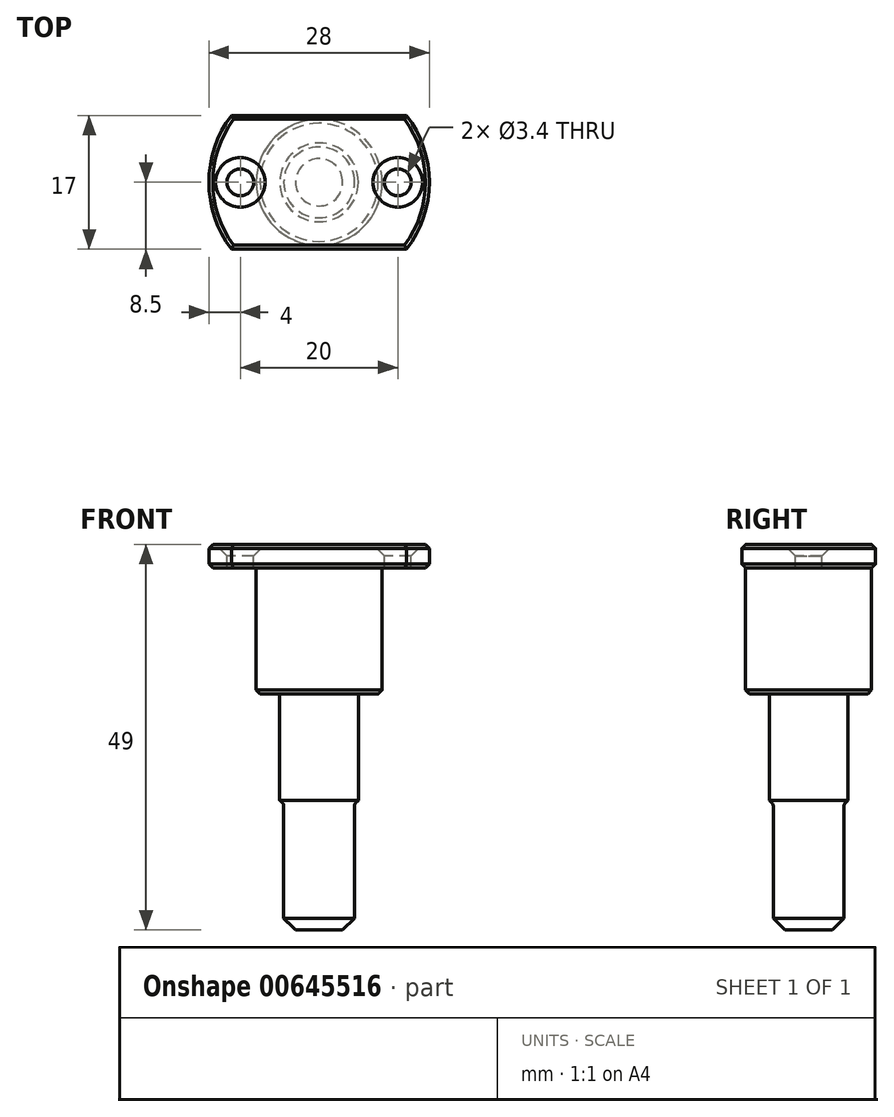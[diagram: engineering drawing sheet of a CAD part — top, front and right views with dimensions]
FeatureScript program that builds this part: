
annotation { "Feature Type Name" : "Feature", "Feature Type Description" : "" }
export const myFeature = defineFeature(function(context is Context, id is Id, definition is map)
    precondition{}
    {
        {
            var Q0;
            Q0=qCreatedBy(makeId("Top.planeOp"),FACE);
            var sketch = newSketch(context, id + "F0", { "sketchPlane" : qUnion([Q0])});
            skCircle(sketch, "E0", {"center": v(0, 0) * mm, "radius": 14 * mm});
            skLineSegment(sketch, "E1", {"start": v(14, 0) * mm, "end": v(14, 8.5) * mm});
            skLineSegment(sketch, "E2.bottom", {"start": v(0, 0) * mm, "end": v(14, 0) * mm});
            skLineSegment(sketch, "E2.top", {"start": v(0, 8.5) * mm, "end": v(14, 8.5) * mm});
            skLineSegment(sketch, "E2.left", {"start": v(0, 0) * mm, "end": v(0, 8.5) * mm});
            skLineSegment(sketch, "E3.MirrorCS", {"start": v(-14, 0) * mm, "end": v(-14, 8.5) * mm});
            skLineSegment(sketch, "E4.MirrorCS", {"start": v(0, 8.5) * mm, "end": v(-14, 8.5) * mm});
            skLineSegment(sketch, "E5.MirrorCS", {"start": v(0, 0) * mm, "end": v(-14, 0) * mm});
            skLineSegment(sketch, "E6.MirrorCS", {"start": v(14, 0) * mm, "end": v(14, -8.5) * mm});
            skLineSegment(sketch, "E7.MirrorCS", {"start": v(-14, 0) * mm, "end": v(-14, -8.5) * mm});
            skLineSegment(sketch, "E8.MirrorCS", {"start": v(0, -8.5) * mm, "end": v(-14, -8.5) * mm});
            skLineSegment(sketch, "E9.MirrorCS", {"start": v(0, -8.5) * mm, "end": v(14, -8.5) * mm});
            skLineSegment(sketch, "E10.MirrorCS", {"start": v(0, 0) * mm, "end": v(0, -8.5) * mm});
            skSolve(sketch);
        }
        {
            var Q0;
            {var subQ0=sQuery(id+"F0.wireOp",EDGE,"E2.left");Q0=makeQuery(id+"F0.imprint","IMPRINT",FACE,{"disambiguationData":[TD([[makeQuery(id+"F0.imprint","IMPRINT",EDGE,{"derivedFrom":subQ0}),1.0]])]});}
            var Q1;
            {var subQ0=sQuery(id+"F0.wireOp",EDGE,"E5.MirrorCS");Q1=makeQuery(id+"F0.imprint","IMPRINT",FACE,{"disambiguationData":[TD([[makeQuery(id+"F0.imprint","IMPRINT",EDGE,{"derivedFrom":subQ0}),1.0]])]});}
            var Q2;
            {var subQ0=sQuery(id+"F0.wireOp",EDGE,"E2.bottom");Q2=makeQuery(id+"F0.imprint","IMPRINT",FACE,{"disambiguationData":[TD([[makeQuery(id+"F0.imprint","IMPRINT",EDGE,{"derivedFrom":subQ0}),-1.0]])]});}
            var Q3;
            {var subQ0=sQuery(id+"F0.wireOp",EDGE,"E2.bottom");Q3=makeQuery(id+"F0.imprint","IMPRINT",FACE,{"disambiguationData":[TD([[makeQuery(id+"F0.imprint","IMPRINT",EDGE,{"derivedFrom":subQ0}),1.0]])]});}
            extrude(context, id + "F1", {"entities" : qUnion([Q0, Q1, Q2, Q3]), "depth" : 3 * mm, "offsetDistance" : 25 * mm});
        }
        {
            var Q0;
            Q0=makeQuery(id+"F1.opExtrude","CAP_FACE",FACE,{"disambiguationData":[OSD([sQuery(id+"F0.wireOp",EDGE,"E2.top"),sQuery(id+"F0.wireOp",EDGE,"E4.MirrorCS"),sQuery(id+"F0.wireOp",EDGE,"E8.MirrorCS"),sQuery(id+"F0.wireOp",EDGE,"E0"),sQuery(id+"F0.wireOp",EDGE,"E9.MirrorCS")])],"isStart":false});
            var sketch = newSketch(context, id + "F2", { "sketchPlane" : qUnion([Q0])});
            skPoint(sketch, "E11", {"position": v(10, 0) * mm});
            skPoint(sketch, "E12.MirrorP", {"position": v(-10, 0) * mm});
            skSolve(sketch);
        }
        {
            var Q0;
            Q0=sQuery(id+"F2.wireOp",VERTEX,"E11");
            var Q1;
            Q1=sQuery(id+"F2.wireOp",VERTEX,"E12.MirrorP");
            var Q2;
            Q2=makeQuery(id+"F1.opExtrude","SWEPT_BODY",BODY,{"disambiguationData":[OSD([sQuery(id+"F0.wireOp",EDGE,"E2.top"),sQuery(id+"F0.wireOp",EDGE,"E4.MirrorCS"),sQuery(id+"F0.wireOp",EDGE,"E8.MirrorCS"),sQuery(id+"F0.wireOp",EDGE,"E0"),sQuery(id+"F0.wireOp",EDGE,"E9.MirrorCS")])]});
            hole(context, id + "F3", {"style" : HoleStyle.C_SINK, "endStyle" : HoleEndStyle.THROUGH, "holeDiameter" : 3.4 * mm, "cSinkDiameter" : 6.3 * mm, "cSinkAngle" : 90 * degree, "majorDiameter" : 5 * mm, "isTappedThrough" : true, "tappedDepth" : 12 * mm, "tapClearance" : 3, "locations" : qUnion([Q0, Q1]), "scope" : qUnion([Q2])});
        }
        {
            var Q0;
            Q0=qCreatedBy(makeId("Top.planeOp"),FACE);
            var sketch = newSketch(context, id + "F4", { "sketchPlane" : qUnion([Q0])});
            skCircle(sketch, "E13", {"center": v(0, 0) * mm, "radius": 8 * mm});
            skSolve(sketch);
        }
        {
            var Q0;
            Q0=makeQuery(id+"F4.imprint","IMPRINT",FACE,{"disambiguationData":[TD([[makeQuery(id+"F4.imprint","IMPRINT",EDGE,{"derivedFrom":sQuery(id+"F4.wireOp",EDGE,"E13")}),1.0]])]});
            extrude(context, id + "F5", {"entities" : qUnion([Q0]), "operationType" : NewBodyOperationType.ADD, "oppositeDirection" : true, "depth" : 16 * mm, "offsetDistance" : 25 * mm});
        }
        {
            var Q0;
            Q0=makeQuery(id+"F5.opExtrude","CAP_FACE",FACE,{"disambiguationData":[OSD([sQuery(id+"F4.wireOp",EDGE,"E13")])],"isStart":false});
            var sketch = newSketch(context, id + "F6", { "sketchPlane" : qUnion([Q0])});
            skCircle(sketch, "E14", {"center": v(0, 0) * mm, "radius": 5 * mm});
            skSolve(sketch);
        }
        {
            var Q0;
            Q0=makeQuery(id+"F6.imprint","IMPRINT",FACE,{"disambiguationData":[TD([[makeQuery(id+"F6.imprint","IMPRINT",EDGE,{"derivedFrom":sQuery(id+"F6.wireOp",EDGE,"E14")}),1.0]])]});
            extrude(context, id + "F7", {"entities" : qUnion([Q0]), "operationType" : NewBodyOperationType.ADD, "depth" : (30 - 16) * mm, "offsetDistance" : 25 * mm});
        }
        {
            var Q0;
            Q0=makeQuery(id+"F7.opExtrude","CAP_FACE",FACE,{"disambiguationData":[OSD([sQuery(id+"F6.wireOp",EDGE,"E14")])],"isStart":false});
            var sketch = newSketch(context, id + "F8", { "sketchPlane" : qUnion([Q0])});
            skCircle(sketch, "E15", {"center": v(0, 0) * mm, "radius": 4.5 * mm});
            skSolve(sketch);
        }
        {
            var Q0;
            Q0=makeQuery(id+"F8.imprint","IMPRINT",FACE,{"disambiguationData":[TD([[makeQuery(id+"F8.imprint","IMPRINT",EDGE,{"derivedFrom":sQuery(id+"F8.wireOp",EDGE,"E15")}),1.0]])]});
            extrude(context, id + "F9", {"entities" : qUnion([Q0]), "operationType" : NewBodyOperationType.ADD, "depth" : (46 - 30) * mm, "offsetDistance" : 25 * mm});
        }
        {
            var Q0;
            Q0=makeQuery(id+"F7.opExtrude","CAP_EDGE",EDGE,{"disambiguationData":[OSD([sQuery(id+"F6.wireOp",EDGE,"E14")])],"isStart":false});
            var Q1;
            Q1=makeQuery(id+"F5.opExtrude","CAP_EDGE",EDGE,{"disambiguationData":[OSD([sQuery(id+"F4.wireOp",EDGE,"E13")])],"isStart":false});
            var Q2;
            {var subQ0=sQuery(id+"F0.wireOp",EDGE,"E0");Q2=makeQuery(id+"F1.opExtrude","CAP_EDGE",EDGE,{"disambiguationData":[OSD([subQ0]),TDD([makeQuery(id+"F0.imprint","IMPRINT",EDGE,{"disambiguationData":[TD([[makeQuery(id+"F0.imprint","INTERSECT",VERTEX,{"derivedFrom":[sQuery(id+"F0.wireOp",EDGE,"E8.MirrorCS"),subQ0]}),1.0]])],"derivedFrom":subQ0}),makeQuery(id+"F0.imprint","IMPRINT",EDGE,{"disambiguationData":[TD([[makeQuery(id+"F0.imprint","INTERSECT",VERTEX,{"derivedFrom":[sQuery(id+"F0.wireOp",EDGE,"E4.MirrorCS"),subQ0]}),-1.0]])],"derivedFrom":subQ0})])],"isStart":true});}
            var Q3;
            Q3=makeQuery(id+"F1.opExtrude","CAP_EDGE",EDGE,{"disambiguationData":[OSD([sQuery(id+"F0.wireOp",EDGE,"E8.MirrorCS"),sQuery(id+"F0.wireOp",EDGE,"E9.MirrorCS")])],"isStart":true});
            var Q4;
            Q4=makeQuery(id+"F1.opExtrude","CAP_EDGE",EDGE,{"disambiguationData":[OSD([sQuery(id+"F0.wireOp",EDGE,"E2.top"),sQuery(id+"F0.wireOp",EDGE,"E4.MirrorCS")])],"isStart":true});
            var Q5;
            {var subQ0=sQuery(id+"F0.wireOp",EDGE,"E0");Q5=makeQuery(id+"F1.opExtrude","CAP_EDGE",EDGE,{"disambiguationData":[OSD([subQ0]),TDD([makeQuery(id+"F0.imprint","IMPRINT",EDGE,{"disambiguationData":[TD([[makeQuery(id+"F0.imprint","INTERSECT",VERTEX,{"derivedFrom":[subQ0,sQuery(id+"F0.wireOp",EDGE,"E9.MirrorCS")]}),-1.0]])],"derivedFrom":subQ0}),makeQuery(id+"F0.imprint","IMPRINT",EDGE,{"disambiguationData":[TD([[makeQuery(id+"F0.imprint","INTERSECT",VERTEX,{"derivedFrom":[sQuery(id+"F0.wireOp",EDGE,"E2.top"),subQ0]}),1.0]])],"derivedFrom":subQ0})])],"isStart":true});}
            chamfer(context, id + "F10", {"entities" : qUnion([Q0, Q1, Q2, Q3, Q4, Q5]), "chamferType" : ChamferType.OFFSET_ANGLE, "width" : 0.5 * mm, "oppositeDirection" : false, "angle" : 45 * degree, "tangentPropagation" : true});
        }
        {
            var Q0;
            Q0=makeQuery(id+"F7.opExtrude","CAP_EDGE",EDGE,{"disambiguationData":[OSD([sQuery(id+"F6.wireOp",EDGE,"E14")])],"isStart":true});
            var Q1;
            Q1=makeQuery(id+"F10.opChamfer","BLEND_EDGE",EDGE,{"blendedFrom":[makeQuery(id+"F7.opExtrude","CAP_EDGE",EDGE,{"disambiguationData":[OSD([sQuery(id+"F6.wireOp",EDGE,"E14")])],"isStart":false}),makeQuery(id+"F9.opExtrude","SWEPT_FACE",FACE,{"disambiguationData":[OSD([sQuery(id+"F8.wireOp",EDGE,"E15")])]})],"blendedInto":[makeQuery(id+"F9.opExtrude","SWEPT_FACE",FACE,{"disambiguationData":[OSD([sQuery(id+"F8.wireOp",EDGE,"E15")])]})]});
            fillet(context, id + "F11", {"entities" : qUnion([Q0, Q1]), "radius" : 0.5 * mm, "tangentPropagation" : true, "allowEdgeOverflow" : false});
        }
        {
            var Q0;
            Q0=makeQuery(id+"F9.opExtrude","CAP_EDGE",EDGE,{"disambiguationData":[OSD([sQuery(id+"F8.wireOp",EDGE,"E15")])],"isStart":false});
            chamfer(context, id + "F12", {"entities" : qUnion([Q0]), "width" : 1.5 * mm, "tangentPropagation" : true});
        }
        {
            var Q0;
            {var subQ0=sQuery(id+"F0.wireOp",EDGE,"E0");Q0=makeQuery(id+"F1.opExtrude","CAP_EDGE",EDGE,{"disambiguationData":[OSD([subQ0]),TDD([makeQuery(id+"F0.imprint","IMPRINT",EDGE,{"disambiguationData":[TD([[makeQuery(id+"F0.imprint","INTERSECT",VERTEX,{"derivedFrom":[sQuery(id+"F0.wireOp",EDGE,"E8.MirrorCS"),subQ0]}),1.0]])],"derivedFrom":subQ0}),makeQuery(id+"F0.imprint","IMPRINT",EDGE,{"disambiguationData":[TD([[makeQuery(id+"F0.imprint","INTERSECT",VERTEX,{"derivedFrom":[sQuery(id+"F0.wireOp",EDGE,"E4.MirrorCS"),subQ0]}),-1.0]])],"derivedFrom":subQ0})])],"isStart":false});}
            var Q1;
            Q1=makeQuery(id+"F1.opExtrude","CAP_EDGE",EDGE,{"disambiguationData":[OSD([sQuery(id+"F0.wireOp",EDGE,"E8.MirrorCS"),sQuery(id+"F0.wireOp",EDGE,"E9.MirrorCS")])],"isStart":false});
            var Q2;
            {var subQ0=sQuery(id+"F0.wireOp",EDGE,"E0");Q2=makeQuery(id+"F1.opExtrude","CAP_EDGE",EDGE,{"disambiguationData":[OSD([subQ0]),TDD([makeQuery(id+"F0.imprint","IMPRINT",EDGE,{"disambiguationData":[TD([[makeQuery(id+"F0.imprint","INTERSECT",VERTEX,{"derivedFrom":[subQ0,sQuery(id+"F0.wireOp",EDGE,"E9.MirrorCS")]}),-1.0]])],"derivedFrom":subQ0}),makeQuery(id+"F0.imprint","IMPRINT",EDGE,{"disambiguationData":[TD([[makeQuery(id+"F0.imprint","INTERSECT",VERTEX,{"derivedFrom":[sQuery(id+"F0.wireOp",EDGE,"E2.top"),subQ0]}),1.0]])],"derivedFrom":subQ0})])],"isStart":false});}
            var Q3;
            Q3=makeQuery(id+"F1.opExtrude","CAP_EDGE",EDGE,{"disambiguationData":[OSD([sQuery(id+"F0.wireOp",EDGE,"E2.top"),sQuery(id+"F0.wireOp",EDGE,"E4.MirrorCS")])],"isStart":false});
            chamfer(context, id + "F13", {"entities" : qUnion([Q0, Q1, Q2, Q3]), "chamferType" : ChamferType.OFFSET_ANGLE, "width" : 0.5 * mm, "oppositeDirection" : true, "angle" : 45 * degree, "tangentPropagation" : true});
        }
    });
